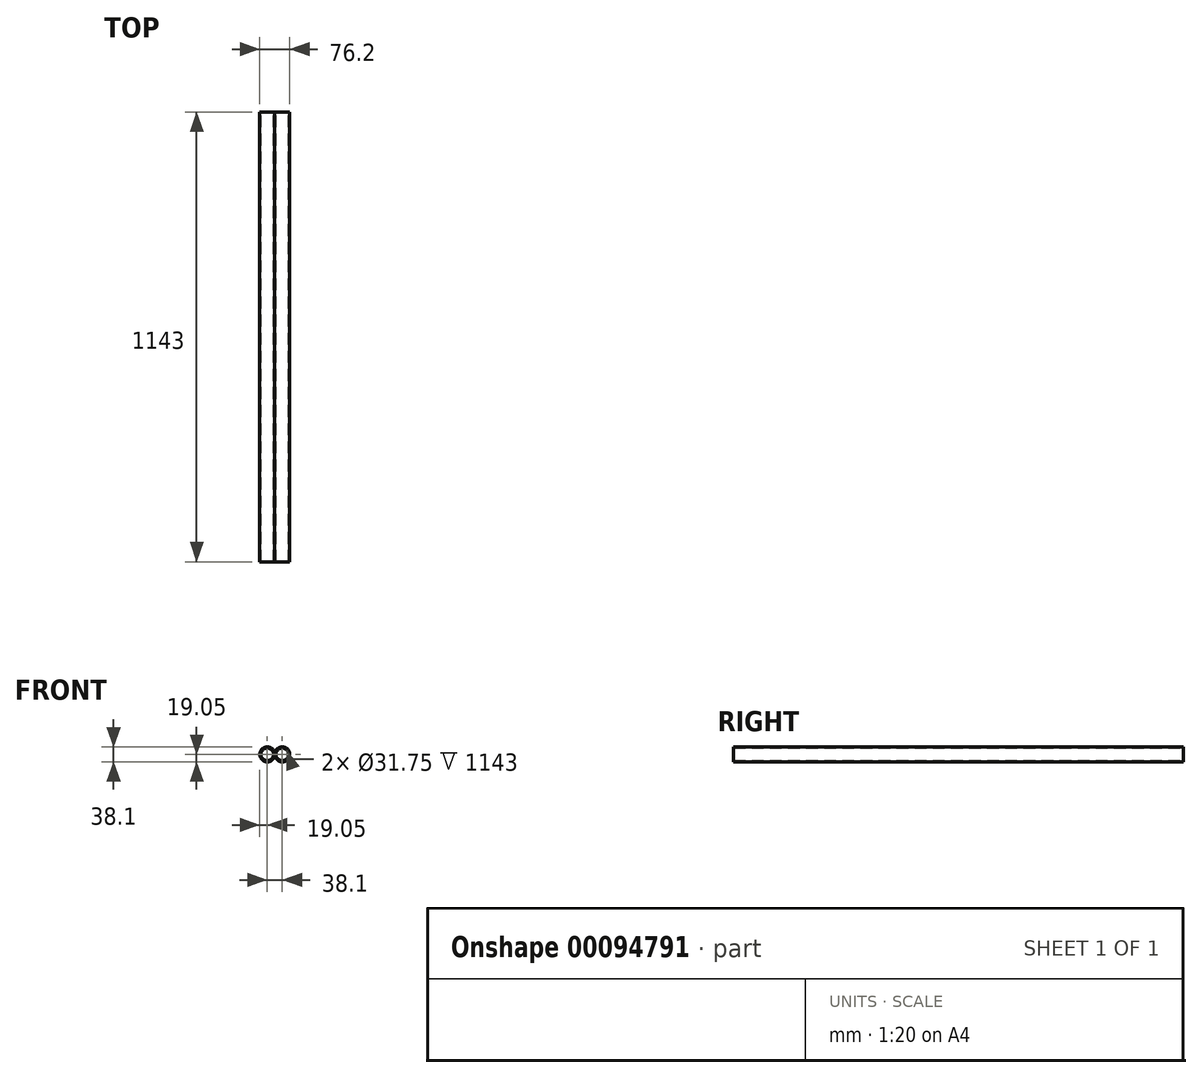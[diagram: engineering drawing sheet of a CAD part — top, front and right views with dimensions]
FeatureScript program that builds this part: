
annotation { "Feature Type Name" : "Feature", "Feature Type Description" : "" }
export const myFeature = defineFeature(function(context is Context, id is Id, definition is map)
    precondition{}
    {
        {
            var Q0;
            Q0=qCreatedBy(makeId("Front.planeOp"),FACE);
            var sketch = newSketch(context, id + "F0", { "sketchPlane" : qUnion([Q0])});
            skLineSegment(sketch, "E0", {"start": v(0, 13.28) * mm, "end": v(0, -18.11) * mm});
            skLineSegment(sketch, "E1", {"start": v(0, 0) * mm, "end": v(19.05, 0) * mm});
            skCircle(sketch, "E2", {"center": v(19.05, 0) * mm, "radius": 19.05 * mm});
            skCircle(sketch, "E3.MirrorC", {"center": v(-19.05, 0) * mm, "radius": 19.05 * mm});
            skCircle(sketch, "E4", {"center": v(-19.05, 0) * mm, "radius": 15.88 * mm});
            skCircle(sketch, "E5", {"center": v(19.05, 0) * mm, "radius": 15.88 * mm});
            skSolve(sketch);
        }
        {
            var Q0;
            Q0 = qSketchRegion(id + "F0", true);
            extrude(context, id + "F1", {"entities" : qUnion([Q0]), "depth" : 1143 * mm});
        }
    });
